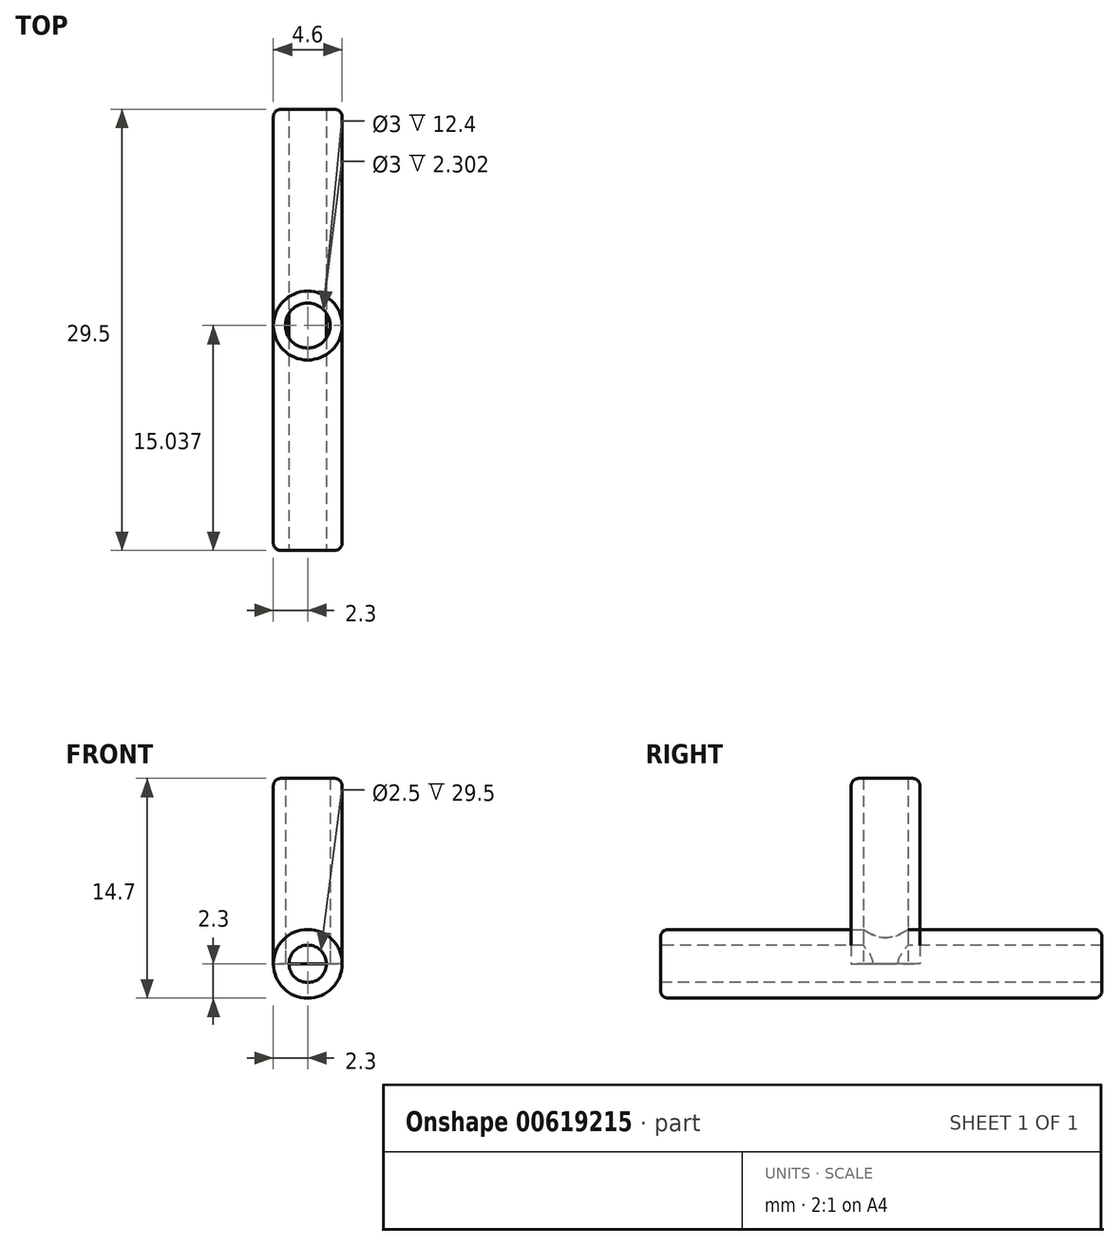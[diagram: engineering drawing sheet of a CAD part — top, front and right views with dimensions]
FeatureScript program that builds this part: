
annotation { "Feature Type Name" : "Feature", "Feature Type Description" : "" }
export const myFeature = defineFeature(function(context is Context, id is Id, definition is map)
    precondition{}
    {
        {
            var Q0;
            Q0=qCreatedBy(makeId("Front.planeOp"),FACE);
            var sketch = newSketch(context, id + "F0", { "sketchPlane" : qUnion([Q0])});
            skCircle(sketch, "E0", {"center": v(0, 0) * mm, "radius": 2.3 * mm});
            skSolve(sketch);
        }
        {
            var Q0;
            Q0=makeQuery(id+"F0.imprint","IMPRINT",FACE,{"disambiguationData":[TD([[makeQuery(id+"F0.imprint","IMPRINT",EDGE,{"derivedFrom":sQuery(id+"F0.wireOp",EDGE,"E0")}),1.0]])]});
            extrude(context, id + "F1", {"entities" : qUnion([Q0]), "depth" : 29.5 * mm, "offsetDistance" : 25.4 * mm});
        }
        {
            var Q0;
            Q0=makeQuery(id+"F1.opExtrude","CAP_FACE",FACE,{"disambiguationData":[OSD([sQuery(id+"F0.wireOp",EDGE,"E0")])],"isStart":false});
            var sketch = newSketch(context, id + "F2", { "sketchPlane" : qUnion([Q0])});
            skCircle(sketch, "E1", {"center": v(0, 0) * mm, "radius": 1.25 * mm, "construction": true});
            skSolve(sketch);
        }
        {
            var Q0;
            Q0=sQuery(id+"F2.wireOp",VERTEX,"E1.center");
            var Q1;
            Q1=makeQuery(id+"F1.opExtrude","SWEPT_BODY",BODY,{"disambiguationData":[OSD([sQuery(id+"F0.wireOp",EDGE,"E0")])]});
            hole(context, id + "F3", {"style" : HoleStyle.SIMPLE, "endStyle" : HoleEndStyle.THROUGH, "holeDiameter" : 2.5 * mm, "majorDiameter" : 6.35 * mm, "isTappedThrough" : true, "tappedDepth" : 12.7 * mm, "tapClearance" : 3, "locations" : qUnion([Q0]), "scope" : qUnion([Q1])});
        }
        {
            var Q0;
            Q0=qCreatedBy(makeId("Top.planeOp"),FACE);
            var sketch = newSketch(context, id + "F4", { "sketchPlane" : qUnion([Q0])});
            skLineSegment(sketch, "E2", {"start": v(0, -16.76) * mm, "end": v(0, -12.16) * mm, "construction": true});
            skCircle(sketch, "E3", {"center": v(0, -14.46) * mm, "radius": 2.3 * mm});
            skCircle(sketch, "E4", {"center": v(0, -14.46) * mm, "radius": 1.5 * mm, "construction": true});
            skSolve(sketch);
        }
        {
            var Q0;
            Q0 = qSketchRegion(id + "F4", true);
            extrude(context, id + "F5", {"entities" : qUnion([Q0]), "depth" : 12.4 * mm, "offsetDistance" : 25.4 * mm});
        }
        {
            var Q0;
            Q0=qCreatedBy(makeId("Top.planeOp"),FACE);
            var sketch = newSketch(context, id + "F6", { "sketchPlane" : qUnion([Q0])});
            skCircle(sketch, "E5", {"center": v(0, -14.46) * mm, "radius": 1.5 * mm});
            skSolve(sketch);
        }
        {
            var Q0;
            Q0 = qSketchRegion(id + "F6", true);
            extrude(context, id + "F7", {"entities" : qUnion([Q0]), "operationType" : NewBodyOperationType.REMOVE, "depth" : 12.4 * mm, "offsetDistance" : 25 * mm});
        }
        {
            var Q0;
            Q0=makeQuery(id+"F5.opExtrude","CAP_EDGE",EDGE,{"disambiguationData":[OSD([sQuery(id+"F4.wireOp",EDGE,"E3")])],"isStart":false});
            fillet(context, id + "F8", {"entities" : qUnion([Q0]), "radius" : 0.5 * mm, "tangentPropagation" : true, "allowEdgeOverflow" : false});
        }
        {
            var Q0;
            Q0=makeQuery(id+"F1.opExtrude","CAP_EDGE",EDGE,{"disambiguationData":[OSD([sQuery(id+"F0.wireOp",EDGE,"E0")])],"isStart":false});
            fillet(context, id + "F9", {"entities" : qUnion([Q0]), "radius" : 0.5 * mm, "tangentPropagation" : true, "allowEdgeOverflow" : false});
        }
        {
            var Q0;
            Q0=makeQuery(id+"F1.opExtrude","CAP_EDGE",EDGE,{"disambiguationData":[OSD([sQuery(id+"F0.wireOp",EDGE,"E0")])],"isStart":true});
            fillet(context, id + "F10", {"entities" : qUnion([Q0]), "radius" : 0.5 * mm, "tangentPropagation" : true, "allowEdgeOverflow" : false});
        }
    });
